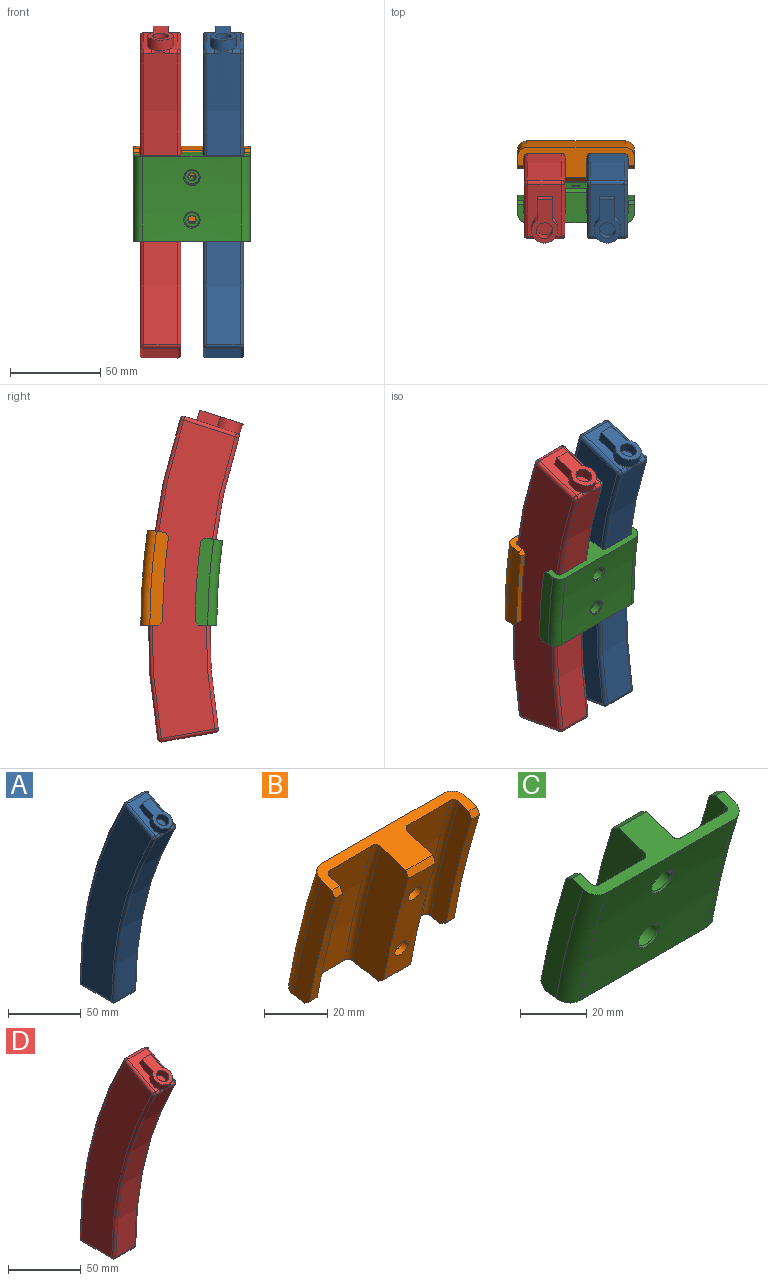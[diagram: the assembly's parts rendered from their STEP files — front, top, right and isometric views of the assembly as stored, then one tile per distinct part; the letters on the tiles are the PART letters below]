
ASSEMBLY  parts=4 mates=4
PART A: 36 faces, bbox 22.5x107.6x188.6 mm
  f0: cylinder r=374mm len=172.21mm, axis (1,0,0), area 3315.6mm2, adj f19,f20,f27,f28
  f1: plane 26.47x18.5mm, normal (0,-0.47,0.88), area 311.3mm2, adj f6,f7,f8,f10,f15,f21,f28,f32
  f2: cylinder r=340mm len=158.01mm, axis (1,0,0), area 3018.2mm2, adj f13,f15,f17,f25,f31,f34,f35
  f3: plane 30x18.5mm, normal (0,0,-1), area 555mm2, adj f18,f19,f25,f26
  f4: plane 171.29x69.29mm, normal (-1,0,0), area 5127.4mm2, adj f17,f18,f20,f21
  f5: plane 171.29x69.29mm, normal (1,0,0), area 5127.4mm2, adj f26,f27,f31,f32
  f6: plane 13.42x10.94mm, normal (-1,0,0), area 72mm2, adj f1,f7,f10,f11
  f7: plane 8.3x5.29mm, normal (0,0.88,0.47), area 49.8mm2, adj f1,f6,f8,f11
  f8: plane 13.42x10.94mm, normal (1,0,0), area 72mm2, adj f1,f7,f10,f11
  f9: cylinder r=4.5mm len=10.76mm, axis (0,0.47,-0.88), area 169.6mm2, adj f11,f12
  f10: cylinder r=7.25mm len=14.5mm, axis (0,0.47,-0.88), area 220.3mm2, adj f1,f6,f8,f11,f13,f35
  f11: plane 22.24x14.5mm, normal (0,-0.47,0.88), area 193.8mm2, adj f6,f7,f8,f9,f10
  f12: plane 9x7.94mm, normal (0,-0.47,0.88), area 63.6mm2, adj f9
  f13: bspline ~5.62x2.84mm, area 4.8mm2, adj f2,f10,f15
  f14: sphere r=2mm, area 6.3mm2, adj f18,f19,f20
  f15: cylinder r=2mm len=4.26mm, axis (1,0,0), area 13.3mm2, adj f1,f2,f13,f16
  f16: sphere r=2mm, area 5.8mm2, adj f15,f17,f21
  f17: torus R=342mm, axis (-1,0,0), area 511.9mm2, adj f2,f4,f16,f22
  f18: cylinder r=2mm len=30mm, axis (0,-1,0), area 94.2mm2, adj f3,f4,f14,f22
  f19: cylinder r=2mm len=18.5mm, axis (1,0,0), area 58.3mm2, adj f0,f3,f14,f23
  f20: torus R=372mm, axis (-1,0,0), area 561.9mm2, adj f0,f4,f14,f24
  f21: cylinder r=2mm len=27.41mm, axis (0,0.88,0.47), area 94.2mm2, adj f1,f4,f16,f24
  f22: sphere r=2mm, area 6.3mm2, adj f17,f18,f25
  f23: sphere r=2mm, area 6.3mm2, adj f19,f26,f27
  f24: sphere r=2mm, area 6.1mm2, adj f20,f21,f28
  f25: cylinder r=2mm len=18.5mm, axis (1,0,0), area 57.9mm2, adj f2,f3,f22,f29
  f26: cylinder r=2mm len=30mm, axis (0,1,0), area 94.2mm2, adj f3,f5,f23,f29
  f27: torus R=372mm, axis (-1,0,0), area 561.9mm2, adj f0,f5,f23,f30
  f28: cylinder r=2mm len=18.5mm, axis (1,0,0), area 58.3mm2, adj f0,f1,f24,f30
  f29: sphere r=2mm, area 6.3mm2, adj f25,f26,f31
  f30: sphere r=2mm, area 7mm2, adj f27,f28,f32
  f31: torus R=342mm, axis (-1,0,0), area 511.9mm2, adj f2,f5,f29,f33
  f32: cylinder r=2mm len=27.41mm, axis (0,-0.88,-0.47), area 94.2mm2, adj f1,f5,f30,f33
  f33: sphere r=2mm, area 5.8mm2, adj f31,f32,f34
  f34: cylinder r=2mm len=4.26mm, axis (1,0,0), area 13.3mm2, adj f1,f2,f33,f35
  f35: bspline ~5.62x2.84mm, area 4.8mm2, adj f2,f10,f34
PART B: 50 faces, bbox 64.7x31.2x54.5 mm
  f0: plane 52.48x25mm, normal (1,0,0), area 570.6mm2, adj f1,f3,f5,f23,f24,f25,f35,f36
  f1: cylinder r=359mm len=44.75mm, axis (-1,0,0), area 498.4mm2, adj f0,f9,f21,f33,f46,f48
  f2: cylinder r=378mm len=54.6mm, axis (1,0,0), area 2881.7mm2, adj f3,f5,f42,f43
  f3: plane 64.6x16.17mm, normal (0,-0.31,0.95), area 425.8mm2, adj f0,f2,f4,f6,f8,f9,f10,f11
  f4: cylinder r=374.5mm len=50.7mm, axis (1,0,0), area 1004mm2, adj f3,f5,f40,f41
  f5: plane 64.6x16.75mm, normal (0,0.17,-0.98), area 425.8mm2, adj f0,f2,f4,f6,f8,f9,f10,f11
  f6: plane 51.27x18.34mm, normal (1,0,0), area 341.6mm2, adj f3,f5,f7,f40,f44,f45
  f7: cylinder r=366mm len=45.69mm, axis (1,0,0), area 164.9mm2, adj f6,f8,f44,f45
  f8: plane 51.36x18.64mm, normal (-1,0,0), area 357.2mm2, adj f3,f5,f7,f43,f44,f45
  f9: plane 52.48x25mm, normal (-1,0,0), area 695.9mm2, adj f1,f3,f5,f41,f46,f48
  f10: cylinder r=374.5mm len=50.7mm, axis (-1,0,0), area 1004mm2, adj f3,f5,f38,f39
  f11: plane 51.27x18.34mm, normal (-1,0,0), area 341.6mm2, adj f3,f5,f12,f39,f47,f49
  f12: cylinder r=366mm len=45.69mm, axis (-1,0,0), area 164.9mm2, adj f11,f13,f47,f49
  f13: plane 51.36x18.64mm, normal (1,0,0), area 357.2mm2, adj f3,f5,f12,f42,f47,f49
  f14: cylinder r=2.25mm len=6.33mm, axis (0,0.98,0.21), area 77.9mm2, adj f19,f21
  f15: plane 6.19x5.38mm, normal (0,-0.21,0.98), area 34.1mm2, adj f18,f19,f20,f24
  f16: plane 6.19x5.38mm, normal (0,0.21,-0.98), area 34.1mm2, adj f17,f19,f20,f23
  f17: plane 6.17x4.86mm, normal (0.87,0.1,-0.49), area 24.1mm2, adj f16,f18,f19,f20
  f18: plane 6.17x4.86mm, normal (0.87,-0.1,0.49), area 24.1mm2, adj f15,f17,f19,f20
  f19: plane 8.39x7.43mm, normal (0,0.98,0.21), area 39.5mm2, adj f14,f15,f16,f17,f18,f25
  f20: plane 8.39x7.43mm, normal (0,-0.98,-0.21), area 55.4mm2, adj f15,f16,f17,f18,f22
  f21: bspline ~5.96x5.79mm, area 34.8mm2, adj f1,f14
  f22: plane 8.91x2.5mm, normal (0.34,-0.92,-0.2), area 17.7mm2, adj f20,f23,f24,f38
  f23: plane 6.8x2.01mm, normal (0.34,0.2,-0.92), area 13.3mm2, adj f0,f16,f22,f25,f38
  f24: plane 6.8x2.01mm, normal (0.34,-0.2,0.92), area 13.3mm2, adj f0,f15,f22,f25,f38
  f25: plane 8.86x2.44mm, normal (0.34,0.92,0.2), area 17.7mm2, adj f0,f19,f23,f24
  f26: cylinder r=2.25mm len=6.54mm, axis (0,0.96,0.28), area 77.9mm2, adj f31,f33
  f27: plane 6.19x5.29mm, normal (0,-0.28,0.96), area 34.1mm2, adj f30,f31,f32,f36
  f28: plane 6.19x5.29mm, normal (0,0.28,-0.96), area 34.1mm2, adj f29,f31,f32,f35
  f29: plane 6.33x5.17mm, normal (0.87,0.14,-0.48), area 24.1mm2, adj f28,f30,f31,f32
  f30: plane 6.33x5.17mm, normal (0.87,-0.14,0.48), area 24.1mm2, adj f27,f29,f31,f32
  f31: plane 8.39x7.31mm, normal (0,0.96,0.28), area 39.5mm2, adj f26,f27,f28,f29,f30,f37
  f32: plane 8.39x7.31mm, normal (0,-0.96,-0.28), area 55.4mm2, adj f27,f28,f29,f30,f34
  f33: bspline ~5.96x5.69mm, area 34.8mm2, adj f1,f26
  f34: plane 8.76x3.05mm, normal (0.34,-0.9,-0.26), area 17.7mm2, adj f32,f35,f36,f38
  f35: plane 6.69x2.42mm, normal (0.34,0.26,-0.9), area 13.3mm2, adj f0,f28,f34,f37,f38
  f36: plane 6.69x2.42mm, normal (0.34,-0.26,0.9), area 13.3mm2, adj f0,f27,f34,f37,f38
  f37: plane 8.71x3mm, normal (0.34,0.9,0.26), area 17.7mm2, adj f0,f31,f35,f36
  f38: torus R=372.7mm, axis (-1,0,0), area 146.6mm2, adj f0,f3,f5,f10,f22,f23,f24,f34
  f39: torus R=372.7mm, axis (1,0,0), area 147.6mm2, adj f3,f5,f10,f11
  f40: torus R=372.7mm, axis (-1,0,0), area 147.6mm2, adj f3,f4,f5,f6
  f41: torus R=372.7mm, axis (1,0,0), area 147.6mm2, adj f3,f4,f5,f9
  f42: torus R=373mm, axis (1,0,0), area 412.5mm2, adj f2,f3,f5,f13
  f43: torus R=373mm, axis (-1,0,0), area 412.5mm2, adj f2,f3,f5,f8
  f44: plane 3.5x2.51mm, normal (0,-0.89,0.46), area 9.9mm2, adj f3,f6,f7,f8
  f45: plane 3.5x2.32mm, normal (0,-0.57,-0.82), area 9.9mm2, adj f5,f6,f7,f8
  f46: plane 12x2.32mm, normal (0,-0.57,-0.82), area 33.8mm2, adj f0,f1,f5,f9
  f47: plane 3.5x2.32mm, normal (0,-0.57,-0.82), area 9.9mm2, adj f5,f11,f12,f13
  f48: plane 12x2.51mm, normal (0,-0.89,0.46), area 33.8mm2, adj f0,f1,f3,f9
  f49: plane 3.5x2.51mm, normal (0,-0.89,0.46), area 9.9mm2, adj f3,f11,f12,f13
PART C: 36 faces, bbox 64.6x29.7x50.7 mm
  f0: cylinder r=336mm len=54.6mm, axis (-1,0,0), area 2434.6mm2, adj f2,f3,f18,f23,f28,f29
  f1: cylinder r=355mm len=44.16mm, axis (1,0,0), area 498.8mm2, adj f8,f13,f17,f22,f31,f34
  f2: plane 64.6x16.16mm, normal (0,-0.31,0.95), area 425.5mm2, adj f0,f4,f6,f7,f8,f9,f11,f12
  f3: plane 64.6x16.74mm, normal (0,0.17,-0.98), area 425.5mm2, adj f0,f4,f6,f7,f8,f9,f11,f12
  f4: cylinder r=339.5mm len=45.96mm, axis (-1,0,0), area 910.1mm2, adj f2,f3,f24,f25
  f5: cylinder r=348mm len=43.21mm, axis (-1,0,0), area 156mm2, adj f6,f7,f30,f35
  f6: plane 47.7x18.05mm, normal (1,0,0), area 332.7mm2, adj f2,f3,f5,f28,f30,f35
  f7: plane 47.65x17.76mm, normal (-1,0,0), area 318.4mm2, adj f2,f3,f5,f25,f30,f35
  f8: plane 49.82x24.66mm, normal (1,0,0), area 661.9mm2, adj f1,f2,f3,f24,f31,f34
  f9: cylinder r=339.5mm len=45.96mm, axis (1,0,0), area 910.1mm2, adj f2,f3,f26,f27
  f10: cylinder r=348mm len=43.21mm, axis (1,0,0), area 156mm2, adj f11,f12,f32,f33
  f11: plane 47.7x18.05mm, normal (-1,0,0), area 332.7mm2, adj f2,f3,f10,f29,f32,f33
  f12: plane 47.65x17.76mm, normal (1,0,0), area 318.4mm2, adj f2,f3,f10,f26,f32,f33
  f13: plane 49.82x24.66mm, normal (-1,0,0), area 661.9mm2, adj f1,f2,f3,f27,f31,f34
  f14: cylinder r=2.25mm len=14.13mm, axis (0,0.98,0.21), area 190.7mm2, adj f15,f17
  f15: plane 8x7.83mm, normal (0,-0.98,-0.21), area 34.4mm2, adj f14,f16
  f16: cylinder r=4mm len=8.76mm, axis (0,0.98,0.21), area 113.5mm2, adj f15,f18
  f17: bspline ~5.51x5.4mm, area 11.3mm2, adj f1,f14
  f18: bspline ~9.01x8.79mm, area 19mm2, adj f0,f16
  f19: cylinder r=2.25mm len=14.21mm, axis (0,0.96,0.28), area 190.7mm2, adj f20,f22
  f20: plane 8x7.69mm, normal (0,-0.96,-0.28), area 34.4mm2, adj f19,f21
  f21: cylinder r=4mm len=8.94mm, axis (0,0.96,0.28), area 113.5mm2, adj f20,f23
  f22: bspline ~5.51x5.31mm, area 11.3mm2, adj f1,f19
  f23: bspline ~9.01x8.65mm, area 19mm2, adj f0,f21
  f24: torus R=341.3mm, axis (-1,0,0), area 134.3mm2, adj f2,f3,f4,f8
  f25: torus R=341.3mm, axis (1,0,0), area 134.3mm2, adj f2,f3,f4,f7
  f26: torus R=341.3mm, axis (-1,0,0), area 134.3mm2, adj f2,f3,f9,f12
  f27: torus R=341.3mm, axis (1,0,0), area 134.3mm2, adj f2,f3,f9,f13
  f28: torus R=341mm, axis (1,0,0), area 370.5mm2, adj f0,f2,f3,f6
  f29: torus R=341mm, axis (-1,0,0), area 370.5mm2, adj f0,f2,f3,f11
  f30: plane 3.5x2.33mm, normal (0,0.82,-0.57), area 9.9mm2, adj f3,f5,f6,f7
  f31: plane 12x2.33mm, normal (0,0.82,-0.57), area 34mm2, adj f1,f3,f8,f13
  f32: plane 3.5x2.33mm, normal (0,0.82,-0.57), area 9.9mm2, adj f3,f10,f11,f12
  f33: plane 3.5x2.52mm, normal (0,0.46,0.89), area 9.9mm2, adj f2,f10,f11,f12
  f34: plane 12x2.52mm, normal (0,0.46,0.89), area 34mm2, adj f1,f2,f8,f13
  f35: plane 3.5x2.52mm, normal (0,0.46,0.89), area 9.9mm2, adj f2,f5,f6,f7
PART D: 36 faces, bbox 22.5x107.6x188.6 mm
  f0: cylinder r=374mm len=172.21mm, axis (-1,0,0), area 3315.6mm2, adj f19,f20,f27,f28
  f1: plane 26.47x18.5mm, normal (0,-0.47,0.88), area 311.3mm2, adj f6,f7,f8,f10,f15,f21,f28,f32
  f2: cylinder r=340mm len=158.01mm, axis (-1,0,0), area 3018.2mm2, adj f13,f15,f17,f25,f31,f34,f35
  f3: plane 30x18.5mm, normal (0,0,-1), area 555mm2, adj f18,f19,f25,f26
  f4: plane 171.29x69.29mm, normal (1,0,0), area 5127.4mm2, adj f17,f18,f20,f21
  f5: plane 171.29x69.29mm, normal (-1,0,0), area 5127.4mm2, adj f26,f27,f31,f32
  f6: plane 13.42x10.94mm, normal (1,0,0), area 72mm2, adj f1,f7,f10,f11
  f7: plane 8.3x5.29mm, normal (0,0.88,0.47), area 49.8mm2, adj f1,f6,f8,f11
  f8: plane 13.42x10.94mm, normal (-1,0,0), area 72mm2, adj f1,f7,f10,f11
  f9: cylinder r=4.5mm len=10.76mm, axis (0,0.47,-0.88), area 169.6mm2, adj f11,f12
  f10: cylinder r=7.25mm len=14.5mm, axis (0,0.47,-0.88), area 220.3mm2, adj f1,f6,f8,f11,f13,f35
  f11: plane 22.24x14.5mm, normal (0,-0.47,0.88), area 193.8mm2, adj f6,f7,f8,f9,f10
  f12: plane 9x7.94mm, normal (0,-0.47,0.88), area 63.6mm2, adj f9
  f13: bspline ~5.62x2.84mm, area 4.9mm2, adj f2,f10,f15
  f14: sphere r=2mm, area 6.3mm2, adj f18,f19,f20
  f15: cylinder r=2mm len=4.26mm, axis (-1,0,0), area 13.3mm2, adj f1,f2,f13,f16
  f16: sphere r=2mm, area 6.3mm2, adj f15,f17,f21
  f17: torus R=342mm, axis (1,0,0), area 511.9mm2, adj f2,f4,f16,f22
  f18: cylinder r=2mm len=30mm, axis (0,-1,0), area 94.2mm2, adj f3,f4,f14,f22
  f19: cylinder r=2mm len=18.5mm, axis (-1,0,0), area 58.3mm2, adj f0,f3,f14,f23
  f20: torus R=372mm, axis (1,0,0), area 561.9mm2, adj f0,f4,f14,f24
  f21: cylinder r=2mm len=27.41mm, axis (0,0.88,0.47), area 94.2mm2, adj f1,f4,f16,f24
  f22: sphere r=2mm, area 6.3mm2, adj f17,f18,f25
  f23: sphere r=2mm, area 6.3mm2, adj f19,f26,f27
  f24: sphere r=2mm, area 6.3mm2, adj f20,f21,f28
  f25: cylinder r=2mm len=18.5mm, axis (-1,0,0), area 57.9mm2, adj f2,f3,f22,f29
  f26: cylinder r=2mm len=30mm, axis (0,1,0), area 94.2mm2, adj f3,f5,f23,f29
  f27: torus R=372mm, axis (1,0,0), area 561.9mm2, adj f0,f5,f23,f30
  f28: cylinder r=2mm len=18.5mm, axis (-1,0,0), area 58.3mm2, adj f0,f1,f24,f30
  f29: sphere r=2mm, area 6.3mm2, adj f25,f26,f31
  f30: sphere r=2mm, area 6.8mm2, adj f27,f28,f32
  f31: torus R=342mm, axis (1,0,0), area 511.9mm2, adj f2,f5,f29,f33
  f32: cylinder r=2mm len=27.41mm, axis (0,-0.88,-0.47), area 94.2mm2, adj f1,f5,f30,f33
  f33: sphere r=2mm, area 5.8mm2, adj f31,f32,f34
  f34: cylinder r=2mm len=4.26mm, axis (-1,0,0), area 13.3mm2, adj f1,f2,f33,f35
  f35: bspline ~5.62x2.84mm, area 4.9mm2, adj f2,f10,f34
PLACE A rot(axis=(-1,0,0),10deg) t=(-17.15,-6.71,-59.04)mm
PLACE B rot(axis=(-1,0,0),10deg) t=(-17.25,-6.71,-59.04)mm
PLACE C rot(axis=(-1,0,0),10deg) t=(-17.25,-6.71,-59.04)mm
PLACE D rot(axis=(-1,0,0),10deg) t=(-17.4,-6.71,-59.04)mm
MATE fastened D.f0 <-> B.f1  axis (-1,0,0) through (-17.4,-341.55,0)mm
MATE slider B.f26 <-> C.f19  axis (0,0.99,0.1) through (0,17.43,37.73)mm
MATE fastened A.f0 <-> D.f0  axis (1,0,0) through (17.35,-341.55,0)mm
MATE fastened C.f0 <-> D.f0  axis (1,0,0) through (-17.4,-341.55,0)mm
